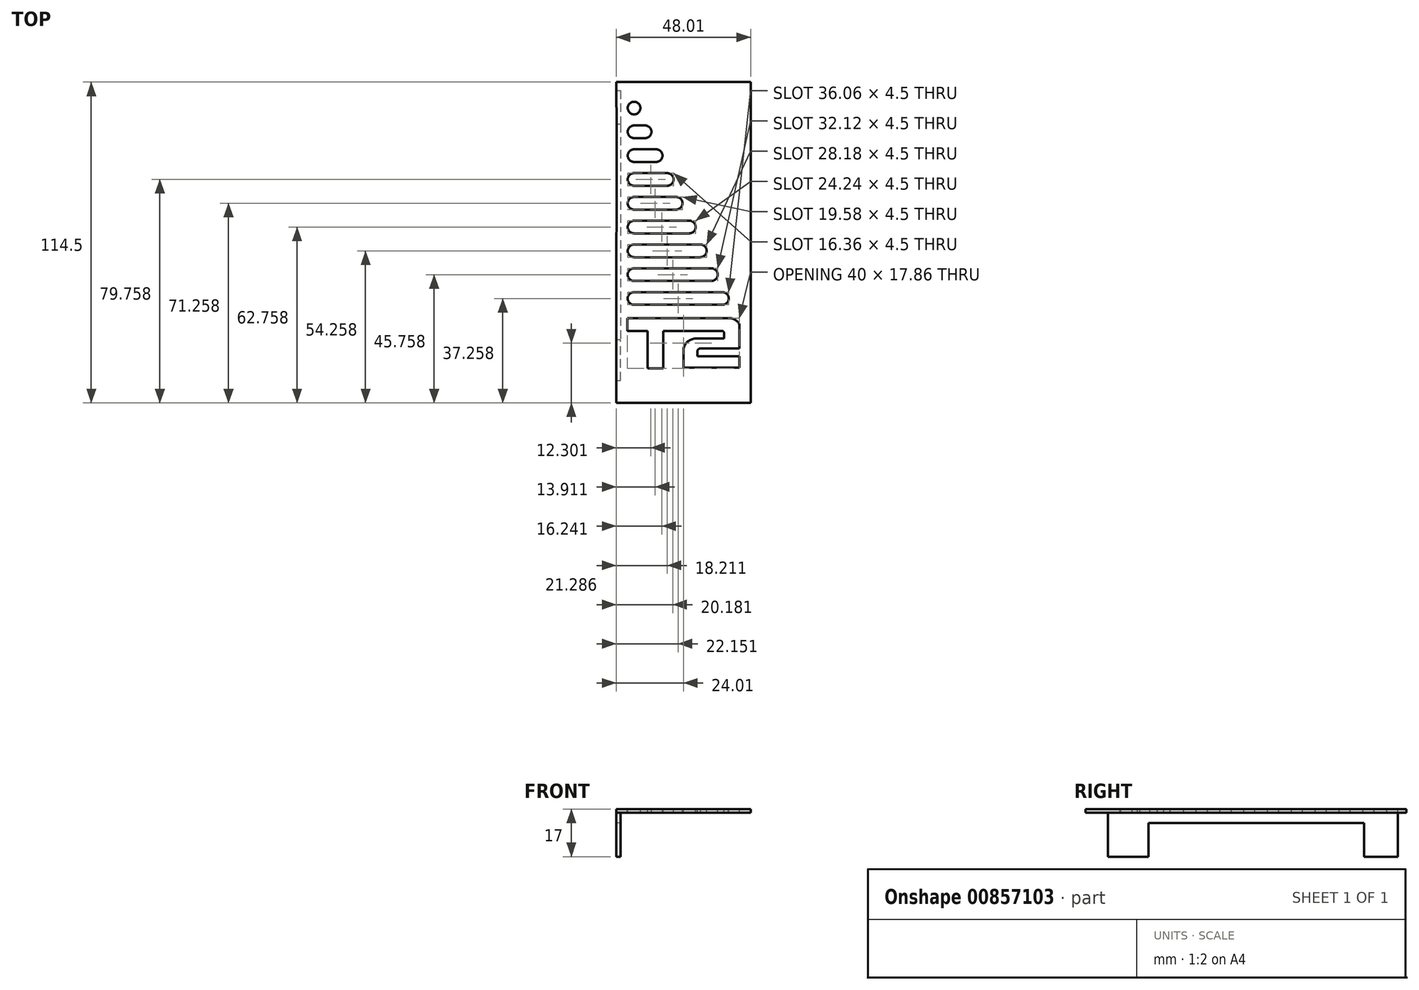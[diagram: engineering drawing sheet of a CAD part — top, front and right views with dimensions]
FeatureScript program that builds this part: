
annotation { "Feature Type Name" : "Feature", "Feature Type Description" : "" }
export const myFeature = defineFeature(function(context is Context, id is Id, definition is map)
    precondition{}
    {
        {
            var Q0;
            Q0=qCreatedBy(makeId("Top.planeOp"),FACE);
            var sketch = newSketch(context, id + "F0", { "sketchPlane" : qUnion([Q0])});
            skLineSegment(sketch, "E0.bottom", {"start": v(-24, 57.25) * mm, "end": v(24, 57.25) * mm});
            skLineSegment(sketch, "E0.right", {"start": v(24, 57.25) * mm, "end": v(24, -57.25) * mm});
            skPoint(sketch, "E0.middle", {"position": v(0, 0) * mm});
            skLineSegment(sketch, "E1", {"start": v(-20, -27.03) * mm, "end": v(-20, -31.53) * mm});
            skLineSegment(sketch, "E2", {"start": v(-12.75, -31.53) * mm, "end": v(-20, -31.53) * mm});
            skLineSegment(sketch, "E3", {"start": v(-12.75, -31.53) * mm, "end": v(-12.75, -44.9) * mm});
            skLineSegment(sketch, "E4", {"start": v(-12.75, -44.9) * mm, "end": v(-7.25, -44.9) * mm});
            skLineSegment(sketch, "E5", {"start": v(19.99, -40.62) * mm, "end": v(4.99, -40.62) * mm});
            skArc(sketch, "E6", {"start": v(4.33, -34.3) * mm, "mid": v(1.6, -35.34) * mm, "end": v(0, -37.8) * mm});
            skArc(sketch, "E7", {"start": v(6.16, -37.76) * mm, "mid": v(5.44, -38.04) * mm, "end": v(4.99, -38.66) * mm});
            skArc(sketch, "E8", {"start": v(20, -29.26) * mm, "mid": v(18.38, -27.56) * mm, "end": v(16.1, -27.03) * mm});
            skLineSegment(sketch, "E9", {"start": v(-20, -27.03) * mm, "end": v(16.1, -27.03) * mm});
            skLineSegment(sketch, "E10", {"start": v(4.99, -38.66) * mm, "end": v(4.99, -40.62) * mm});
            skLineSegment(sketch, "E11", {"start": v(6.16, -37.76) * mm, "end": v(20, -37.76) * mm});
            skLineSegment(sketch, "E12", {"start": v(20, -29.26) * mm, "end": v(20, -37.76) * mm});
            skLineSegment(sketch, "E13", {"start": v(4.33, -34.3) * mm, "end": v(14.5, -34.3) * mm});
            skLineSegment(sketch, "E14", {"start": v(-17.64, -22.24) * mm, "end": v(13.92, -22.24) * mm});
            skLineSegment(sketch, "E15", {"start": v(13.92, -17.74) * mm, "end": v(-17.64, -17.74) * mm});
            skArc(sketch, "E16", {"start": v(-17.64, -17.74) * mm, "mid": v(-19.89, -20) * mm, "end": v(-17.64, -22.24) * mm});
            skArc(sketch, "E17", {"start": v(13.92, -17.74) * mm, "mid": v(16.17, -20) * mm, "end": v(13.92, -22.24) * mm});
            skLineSegment(sketch, "E18", {"start": v(-17.64, -13.74) * mm, "end": v(9.98, -13.74) * mm});
            skLineSegment(sketch, "E19", {"start": v(9.98, -9.24) * mm, "end": v(-17.64, -9.24) * mm});
            skArc(sketch, "E20", {"start": v(-17.64, -9.24) * mm, "mid": v(-19.89, -11.5) * mm, "end": v(-17.64, -13.74) * mm});
            skArc(sketch, "E21", {"start": v(9.98, -9.24) * mm, "mid": v(12.23, -11.5) * mm, "end": v(9.98, -13.74) * mm});
            skLineSegment(sketch, "E22", {"start": v(-17.64, -5.24) * mm, "end": v(6.04, -5.24) * mm});
            skLineSegment(sketch, "E23", {"start": v(6.04, -0.74) * mm, "end": v(-17.64, -0.74) * mm});
            skArc(sketch, "E24", {"start": v(-17.64, -0.74) * mm, "mid": v(-19.89, -3) * mm, "end": v(-17.64, -5.24) * mm});
            skArc(sketch, "E25", {"start": v(6.04, -0.74) * mm, "mid": v(8.3, -3) * mm, "end": v(6.04, -5.24) * mm});
            skLineSegment(sketch, "E26", {"start": v(-17.64, 3.26) * mm, "end": v(2.1, 3.26) * mm});
            skLineSegment(sketch, "E27", {"start": v(2.1, 7.76) * mm, "end": v(-17.64, 7.76) * mm});
            skArc(sketch, "E28", {"start": v(-17.64, 7.76) * mm, "mid": v(-19.89, 5.5) * mm, "end": v(-17.64, 3.26) * mm});
            skArc(sketch, "E29", {"start": v(2.1, 7.76) * mm, "mid": v(4.35, 5.5) * mm, "end": v(2.1, 3.26) * mm});
            skLineSegment(sketch, "E30", {"start": v(-17.64, 11.76) * mm, "end": v(-2.56, 11.76) * mm});
            skLineSegment(sketch, "E31", {"start": v(-2.56, 16.26) * mm, "end": v(-17.64, 16.26) * mm});
            skArc(sketch, "E32", {"start": v(-17.64, 16.26) * mm, "mid": v(-19.89, 14) * mm, "end": v(-17.64, 11.76) * mm});
            skArc(sketch, "E33", {"start": v(-2.56, 16.26) * mm, "mid": v(-0.3, 14) * mm, "end": v(-2.56, 11.76) * mm});
            skLineSegment(sketch, "E34", {"start": v(-17.64, 20.26) * mm, "end": v(-5.78, 20.26) * mm});
            skLineSegment(sketch, "E35", {"start": v(-5.78, 24.76) * mm, "end": v(-17.64, 24.76) * mm});
            skArc(sketch, "E36", {"start": v(-17.64, 24.76) * mm, "mid": v(-19.89, 22.5) * mm, "end": v(-17.64, 20.26) * mm});
            skArc(sketch, "E37", {"start": v(-5.78, 24.76) * mm, "mid": v(-3.53, 22.5) * mm, "end": v(-5.78, 20.26) * mm});
            skLineSegment(sketch, "E38", {"start": v(-17.64, 28.76) * mm, "end": v(-9.72, 28.76) * mm});
            skLineSegment(sketch, "E39", {"start": v(-9.72, 33.26) * mm, "end": v(-17.64, 33.26) * mm});
            skArc(sketch, "E40", {"start": v(-17.64, 33.26) * mm, "mid": v(-19.89, 31) * mm, "end": v(-17.64, 28.76) * mm});
            skArc(sketch, "E41", {"start": v(-9.72, 33.26) * mm, "mid": v(-7.47, 31) * mm, "end": v(-9.72, 28.76) * mm});
            skLineSegment(sketch, "E42", {"start": v(-17.64, 37.26) * mm, "end": v(-13.66, 37.26) * mm});
            skLineSegment(sketch, "E43", {"start": v(-13.66, 41.76) * mm, "end": v(-17.64, 41.76) * mm});
            skArc(sketch, "E44", {"start": v(-17.64, 41.76) * mm, "mid": v(-19.89, 39.5) * mm, "end": v(-17.64, 37.26) * mm});
            skArc(sketch, "E45", {"start": v(-13.66, 41.76) * mm, "mid": v(-11.4, 39.5) * mm, "end": v(-13.66, 37.26) * mm});
            skLineSegment(sketch, "E46", {"start": v(-17.64, 45.76) * mm, "end": v(-17.6, 45.76) * mm});
            skLineSegment(sketch, "E47", {"start": v(-17.6, 50.26) * mm, "end": v(-17.64, 50.26) * mm});
            skArc(sketch, "E48", {"start": v(-17.64, 50.26) * mm, "mid": v(-19.89, 48) * mm, "end": v(-17.64, 45.76) * mm});
            skArc(sketch, "E49", {"start": v(-17.6, 50.26) * mm, "mid": v(-15.35, 48) * mm, "end": v(-17.6, 45.76) * mm});
            skLineSegment(sketch, "E50", {"start": v(-7.25, -44.9) * mm, "end": v(-7.25, -31.53) * mm});
            skLineSegment(sketch, "E51", {"start": v(19.99, -40.62) * mm, "end": v(20, -44.62) * mm});
            skLineSegment(sketch, "E52", {"start": v(0, -37.8) * mm, "end": v(0, -44.62) * mm});
            skLineSegment(sketch, "E53", {"start": v(0, -44.62) * mm, "end": v(20, -44.62) * mm});
            skArc(sketch, "E54", {"start": v(14.5, -32.31) * mm, "mid": v(14.27, -31.76) * mm, "end": v(13.72, -31.53) * mm});
            skLineSegment(sketch, "E55", {"start": v(14.5, -32.31) * mm, "end": v(14.5, -34.3) * mm});
            skLineSegment(sketch, "E56", {"start": v(-7.25, -31.53) * mm, "end": v(13.72, -31.53) * mm});
            skLineSegment(sketch, "E57", {"start": v(-24, -49.25) * mm, "end": v(-22.5, -49.25) * mm});
            skLineSegment(sketch, "E58", {"start": v(-24, -57.25) * mm, "end": v(24, -57.25) * mm});
            skLineSegment(sketch, "E59", {"start": v(-24, 57.25) * mm, "end": v(-24, 54.25) * mm});
            skLineSegment(sketch, "E60", {"start": v(-24, -57.25) * mm, "end": v(-24, -49.25) * mm});
            skLineSegment(sketch, "E61", {"start": v(-24, 54.25) * mm, "end": v(-22.5, 54.25) * mm});
            skLineSegment(sketch, "E62", {"start": v(-22.5, 54.25) * mm, "end": v(-22.5, 42.25) * mm});
            skLineSegment(sketch, "E63", {"start": v(-22.5, 42.25) * mm, "end": v(-23.9, 42.23) * mm});
            skLineSegment(sketch, "E64", {"start": v(-22.5, -34.75) * mm, "end": v(-24, -34.75) * mm});
            skLineSegment(sketch, "E65", {"start": v(-24, -49.25) * mm, "end": v(-24, -34.75) * mm});
            skLineSegment(sketch, "E66", {"start": v(-24, 54.25) * mm, "end": v(-23.9, 42.23) * mm});
            skLineSegment(sketch, "E67", {"start": v(-23.9, 42.23) * mm, "end": v(-24, -34.75) * mm});
            skLineSegment(sketch, "E68", {"start": v(-22.5, -49.25) * mm, "end": v(-22.5, -34.75) * mm});
            skLineSegment(sketch, "E69", {"start": v(-22.5, 42.25) * mm, "end": v(-22.5, -34.75) * mm});
            skSolve(sketch);
        }
        {
            var Q0;
            Q0=makeQuery(id+"F0.imprint","IMPRINT",FACE,{"disambiguationData":[TD([[makeQuery(id+"F0.imprint","IMPRINT",EDGE,{"derivedFrom":sQuery(id+"F0.wireOp",EDGE,"E0.bottom")}),-1.0]])]});
            extrude(context, id + "F1", {"entities" : qUnion([Q0]), "oppositeDirection" : true, "depth" : 1.3 * mm, "offsetDistance" : 25 * mm});
        }
        {
            var Q0;
            Q0=makeQuery(id+"F0.imprint","IMPRINT",FACE,{"disambiguationData":[TD([[makeQuery(id+"F0.imprint","IMPRINT",EDGE,{"derivedFrom":sQuery(id+"F0.wireOp",EDGE,"E61")}),-1.0]])]});
            var Q1;
            Q1=makeQuery(id+"F0.imprint","IMPRINT",FACE,{"disambiguationData":[TD([[makeQuery(id+"F0.imprint","IMPRINT",EDGE,{"derivedFrom":sQuery(id+"F0.wireOp",EDGE,"E57")}),1.0]])]});
            var Q2;
            Q2 = qSketchRegion(id + "F3", true);
            extrude(context, id + "F2", {"entities" : qUnion([Q0, Q1, Q2]), "operationType" : NewBodyOperationType.ADD, "oppositeDirection" : true, "depth" : 17 * mm, "offsetDistance" : 25 * mm});
        }
        {
            var Q0;
            Q0=qCreatedBy(makeId("Right.planeOp"),FACE);
            var sketch = newSketch(context, id + "F3", { "sketchPlane" : qUnion([Q0])});
            skPoint(sketch, "E70", {"position": v(-43.75, -9.5) * mm});
            skPoint(sketch, "E71", {"position": v(48.25, -9.5) * mm});
            skSolve(sketch);
        }
        {
            var Q0;
            Q0=makeQuery(id+"F0.imprint","IMPRINT",FACE,{"disambiguationData":[TD([[makeQuery(id+"F0.imprint","IMPRINT",EDGE,{"derivedFrom":sQuery(id+"F0.wireOp",EDGE,"E63")}),1.0]])]});
            extrude(context, id + "F4", {"entities" : qUnion([Q0]), "operationType" : NewBodyOperationType.ADD, "oppositeDirection" : true, "depth" : 5 * mm, "offsetDistance" : 25 * mm});
        }
    });
